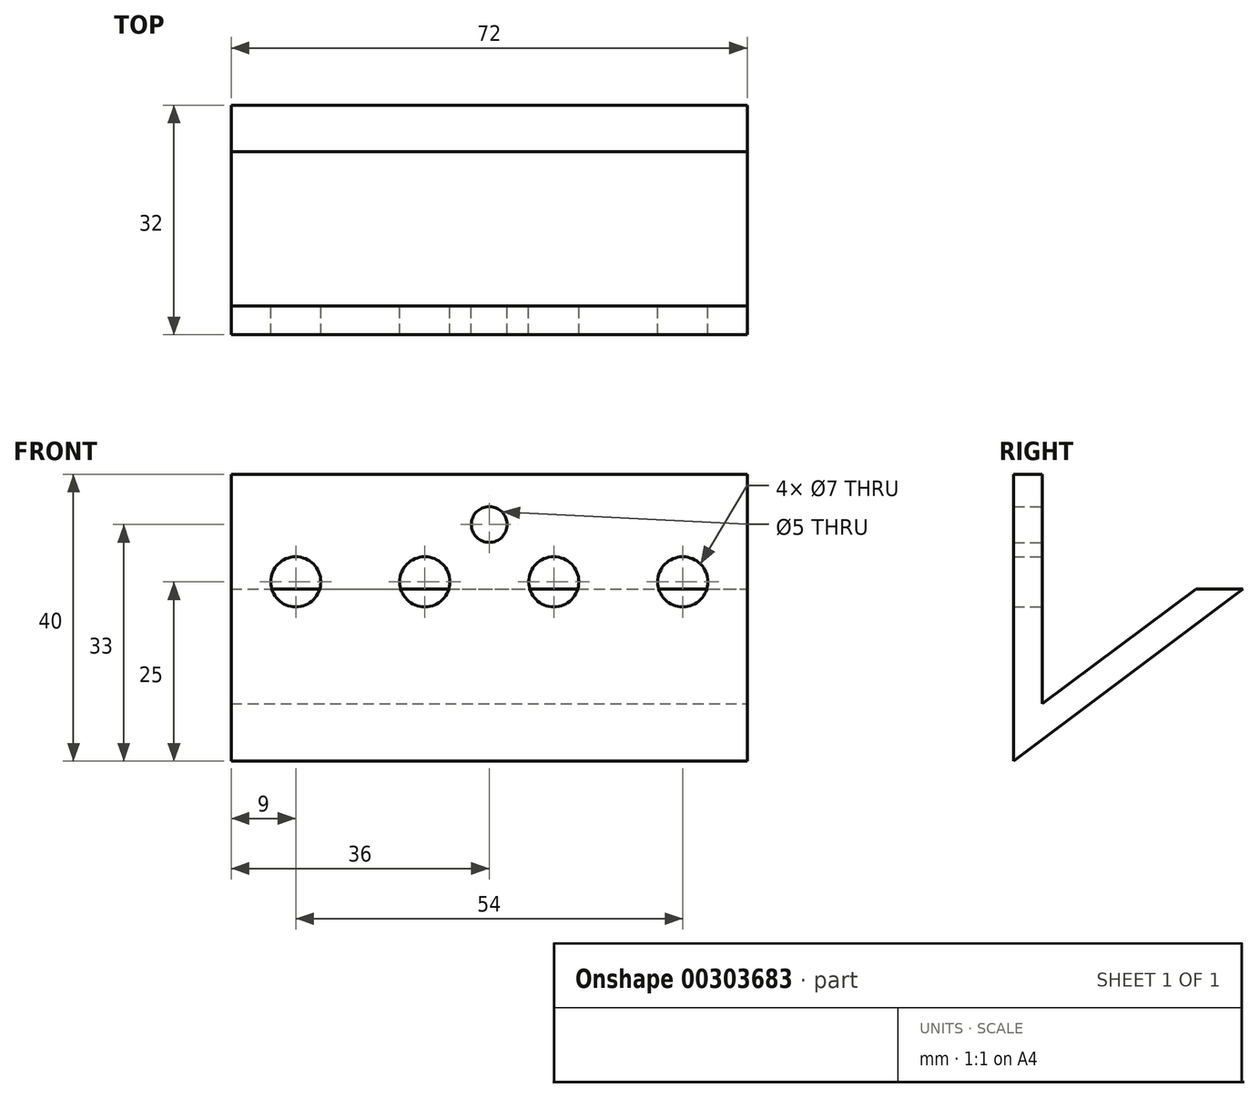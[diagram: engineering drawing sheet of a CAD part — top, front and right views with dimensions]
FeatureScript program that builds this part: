
annotation { "Feature Type Name" : "Feature", "Feature Type Description" : "" }
export const myFeature = defineFeature(function(context is Context, id is Id, definition is map)
    precondition{}
    {
        {
            var Q0;
            Q0=qCreatedBy(makeId("Front.planeOp"),FACE);
            var sketch = newSketch(context, id + "F0", { "sketchPlane" : qUnion([Q0])});
            skLineSegment(sketch, "E0.bottom", {"start": v(-36, 15) * mm, "end": v(36, 15) * mm});
            skLineSegment(sketch, "E0.top", {"start": v(-36, -25) * mm, "end": v(36, -25) * mm});
            skLineSegment(sketch, "E0.left", {"start": v(-36, 15) * mm, "end": v(-36, -25) * mm});
            skLineSegment(sketch, "E0.right", {"start": v(36, 15) * mm, "end": v(36, -25) * mm});
            skPoint(sketch, "E1", {"position": v(-36, 0) * mm});
            skPoint(sketch, "E2", {"position": v(-27, 0) * mm});
            skPoint(sketch, "E3", {"position": v(-9, 0) * mm});
            skPoint(sketch, "E4", {"position": v(9, 0) * mm});
            skPoint(sketch, "E5", {"position": v(27, 0) * mm});
            skCircle(sketch, "E6", {"center": v(-27, 0) * mm, "radius": 3.5 * mm});
            skCircle(sketch, "E7", {"center": v(-9, 0) * mm, "radius": 3.5 * mm});
            skCircle(sketch, "E8", {"center": v(9, 0) * mm, "radius": 3.5 * mm});
            skCircle(sketch, "E9", {"center": v(27, 0) * mm, "radius": 3.5 * mm});
            skPoint(sketch, "E10", {"position": v(0, 8) * mm});
            skCircle(sketch, "E11", {"center": v(0, 8) * mm, "radius": 2.5 * mm});
            skSolve(sketch);
        }
        {
            var Q0;
            Q0=makeQuery(id+"F0.imprint","IMPRINT",FACE,{"disambiguationData":[TD([[makeQuery(id+"F0.imprint","IMPRINT",EDGE,{"derivedFrom":sQuery(id+"F0.wireOp",EDGE,"E0.bottom")}),-1.0]])]});
            extrude(context, id + "F1", {"entities" : qUnion([Q0]), "depth" : 4 * mm});
        }
        {
            var Q0;
            Q0=makeQuery(id+"F1.opExtrude","SWEPT_FACE",FACE,{"disambiguationData":[OSD([sQuery(id+"F0.wireOp",EDGE,"E0.right")])]});
            var sketch = newSketch(context, id + "F2", { "sketchPlane" : qUnion([Q0])});
            skPoint(sketch, "E12", {"position": v(-4, -25) * mm});
            skPoint(sketch, "E13", {"position": v(0, -22) * mm});
            skPoint(sketch, "E14", {"position": v(0, -25) * mm});
            skLineSegment(sketch, "E15", {"start": v(-4, -25) * mm, "end": v(0, -25) * mm});
            skLineSegment(sketch, "E16", {"start": v(0, -25) * mm, "end": v(0, -22) * mm});
            skLineSegment(sketch, "E17", {"start": v(0, -22) * mm, "end": v(-4, -25) * mm});
            skSolve(sketch);
        }
        {
            var Q0;
            Q0=makeQuery(id+"F2.imprint","IMPRINT",FACE,{"disambiguationData":[TD([[makeQuery(id+"F2.imprint","IMPRINT",EDGE,{"derivedFrom":sQuery(id+"F2.wireOp",EDGE,"E15")}),1.0]])]});
            extrude(context, id + "F3", {"entities" : qUnion([Q0]), "operationType" : NewBodyOperationType.REMOVE, "oppositeDirection" : true, "depth" : 72 * mm});
        }
        {
            var Q0;
            Q0=makeQuery(id+"F1.opExtrude","SWEPT_FACE",FACE,{"disambiguationData":[OSD([sQuery(id+"F0.wireOp",EDGE,"E0.right")])]});
            var sketch = newSketch(context, id + "F4", { "sketchPlane" : qUnion([Q0])});
            skPoint(sketch, "E18", {"position": v(-4, -25) * mm});
            skLineSegment(sketch, "E19", {"start": v(-4, -25) * mm, "end": v(28, -1) * mm, "construction": true});
            skPoint(sketch, "E20", {"position": v(28, -1) * mm});
            skPoint(sketch, "E21", {"position": v(21.5, -1) * mm});
            skPoint(sketch, "E22", {"position": v(0, -17) * mm});
            skPoint(sketch, "E23", {"position": v(0, -22) * mm});
            skLineSegment(sketch, "E24", {"start": v(0, -22) * mm, "end": v(28, -1) * mm});
            skLineSegment(sketch, "E25", {"start": v(21.5, -1) * mm, "end": v(28, -1) * mm});
            skLineSegment(sketch, "E26", {"start": v(21.5, -1) * mm, "end": v(0, -17) * mm});
            skLineSegment(sketch, "E27", {"start": v(0, -17) * mm, "end": v(0, -22) * mm});
            skPoint(sketch, "E28", {"position": v(10.75, -9) * mm});
            skLineSegment(sketch, "E29", {"start": v(10.75, -9) * mm, "end": v(16.46, -16.68) * mm, "construction": true});
            skPoint(sketch, "E30", {"position": v(13.1, -12.17) * mm});
            skSolve(sketch);
        }
        {
            var Q0;
            Q0=makeQuery(id+"F4.imprint","IMPRINT",FACE,{"disambiguationData":[TD([[makeQuery(id+"F4.imprint","IMPRINT",EDGE,{"derivedFrom":sQuery(id+"F4.wireOp",EDGE,"E24")}),1.0]])]});
            extrude(context, id + "F5", {"entities" : qUnion([Q0]), "operationType" : NewBodyOperationType.ADD, "oppositeDirection" : true, "depth" : 72 * mm});
        }
    });
